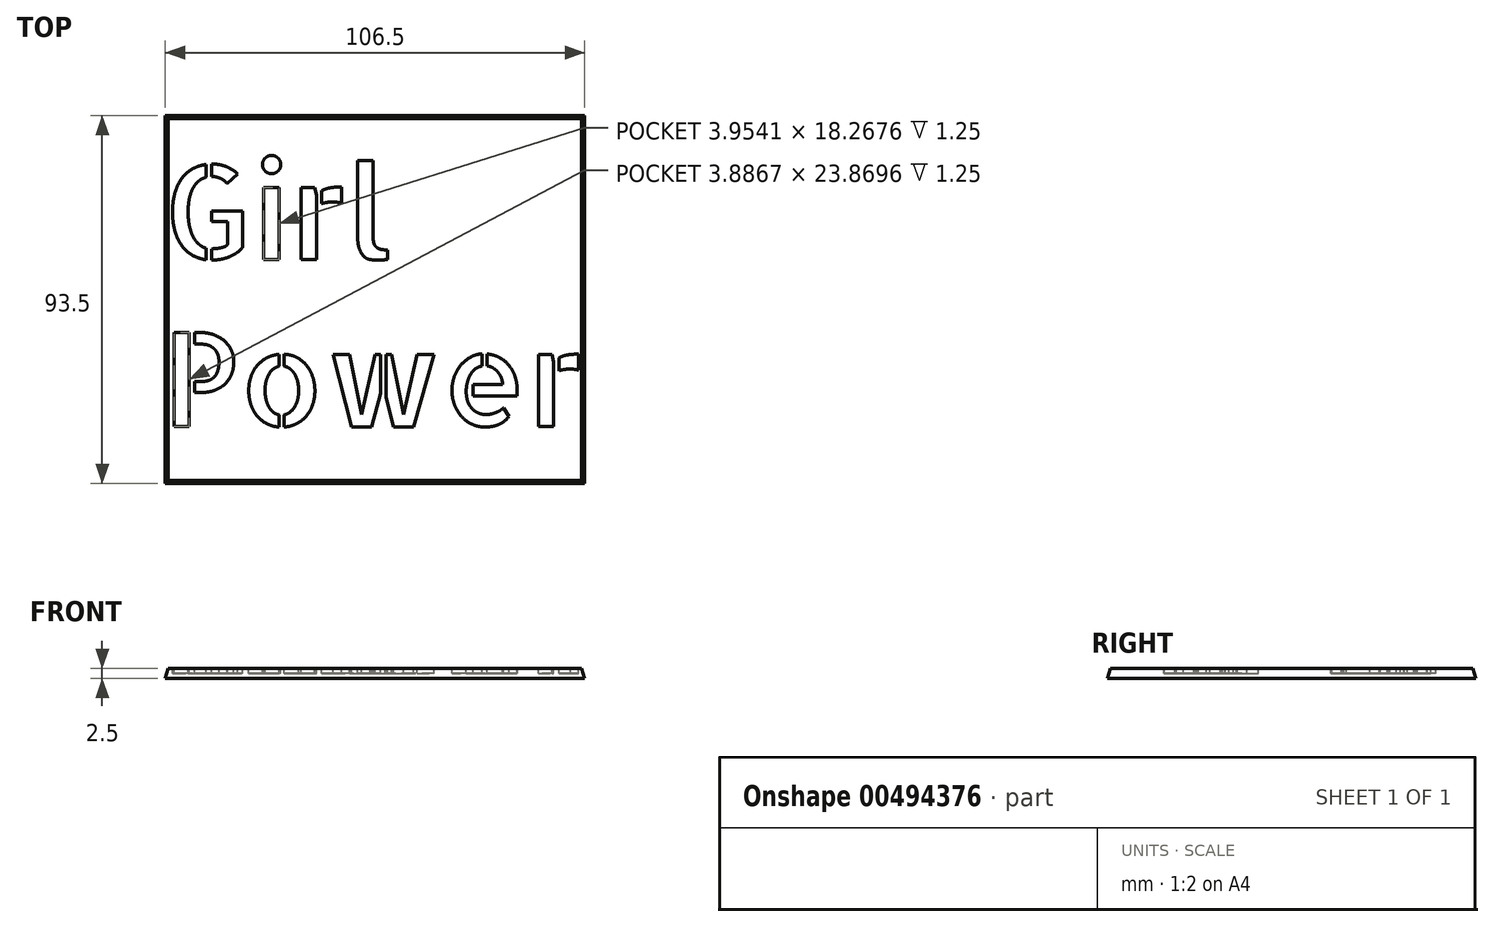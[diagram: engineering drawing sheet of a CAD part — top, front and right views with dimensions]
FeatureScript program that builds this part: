
annotation { "Feature Type Name" : "Feature", "Feature Type Description" : "" }
export const myFeature = defineFeature(function(context is Context, id is Id, definition is map)
    precondition{}
    {
        {
            var Q0;
            Q0=qCreatedBy(makeId("Top.planeOp"),FACE);
            var sketch = newSketch(context, id + "F0", { "sketchPlane" : qUnion([Q0])});
            skLineSegment(sketch, "E0.bottom", {"start": v(54, -47.5) * mm, "end": v(-54, -47.5) * mm});
            skLineSegment(sketch, "E0.top", {"start": v(54, 47.5) * mm, "end": v(-54, 47.5) * mm});
            skLineSegment(sketch, "E0.left", {"start": v(54, -47.5) * mm, "end": v(54, 47.5) * mm});
            skLineSegment(sketch, "E0.right", {"start": v(-54, -47.5) * mm, "end": v(-54, 47.5) * mm});
            skPoint(sketch, "E0.middle", {"position": v(0, 0) * mm});
            skSolve(sketch);
        }
        {
            var Q0;
            Q0 = qSketchRegion(id + "F0", true);
            extrude(context, id + "F1", {"entities" : qUnion([Q0]), "depth" : 2.5 * mm});
        }
        {
            var Q0;
            Q0=makeQuery(id+"F1.opExtrude","CAP_FACE",FACE,{"disambiguationData":[OSD([sQuery(id+"F0.wireOp",EDGE,"E0.bottom"),sQuery(id+"F0.wireOp",EDGE,"E0.top"),sQuery(id+"F0.wireOp",EDGE,"E0.left"),sQuery(id+"F0.wireOp",EDGE,"E0.right")])],"isStart":false});
            var sketch = newSketch(context, id + "F2", { "sketchPlane" : qUnion([Q0])});
            skText(sketch, "E1", { "text": "Girl\nPower", "fontName": "AllertaStencil-Regular.ttf"});
            const initialGuessF2  = {"E1": [-0.054, 0.01019, 1, 0, 0.02388]};
            skSetInitialGuess(sketch, initialGuessF2);
            skSolve(sketch);
        }
        {
            var Q0;
            Q0 = qSketchRegion(id + "F2", true);
            extrude(context, id + "F3", {"entities" : qUnion([Q0]), "operationType" : NewBodyOperationType.REMOVE, "oppositeDirection" : true, "depth" : 1.25 * mm});
        }
        {
            var Q0;
            Q0=makeQuery(id+"F1.opExtrude","CAP_EDGE",EDGE,{"disambiguationData":[OSD([sQuery(id+"F0.wireOp",EDGE,"E0.bottom")])],"isStart":false});
            var Q1;
            Q1=makeQuery(id+"F1.opExtrude","CAP_EDGE",EDGE,{"disambiguationData":[OSD([sQuery(id+"F0.wireOp",EDGE,"E0.right")])],"isStart":false});
            var Q2;
            Q2=makeQuery(id+"F1.opExtrude","CAP_EDGE",EDGE,{"disambiguationData":[OSD([sQuery(id+"F0.wireOp",EDGE,"E0.left")])],"isStart":false});
            var Q3;
            Q3=makeQuery(id+"F1.opExtrude","CAP_EDGE",EDGE,{"disambiguationData":[OSD([sQuery(id+"F0.wireOp",EDGE,"E0.top")])],"isStart":false});
            chamfer(context, id + "F4", {"entities" : qUnion([Q0, Q1, Q2, Q3]), "chamferType" : ChamferType.TWO_OFFSETS, "width1" : 5 * mm, "oppositeDirection" : false, "width2" : 1.5 * mm, "tangentPropagation" : true});
        }
    });
